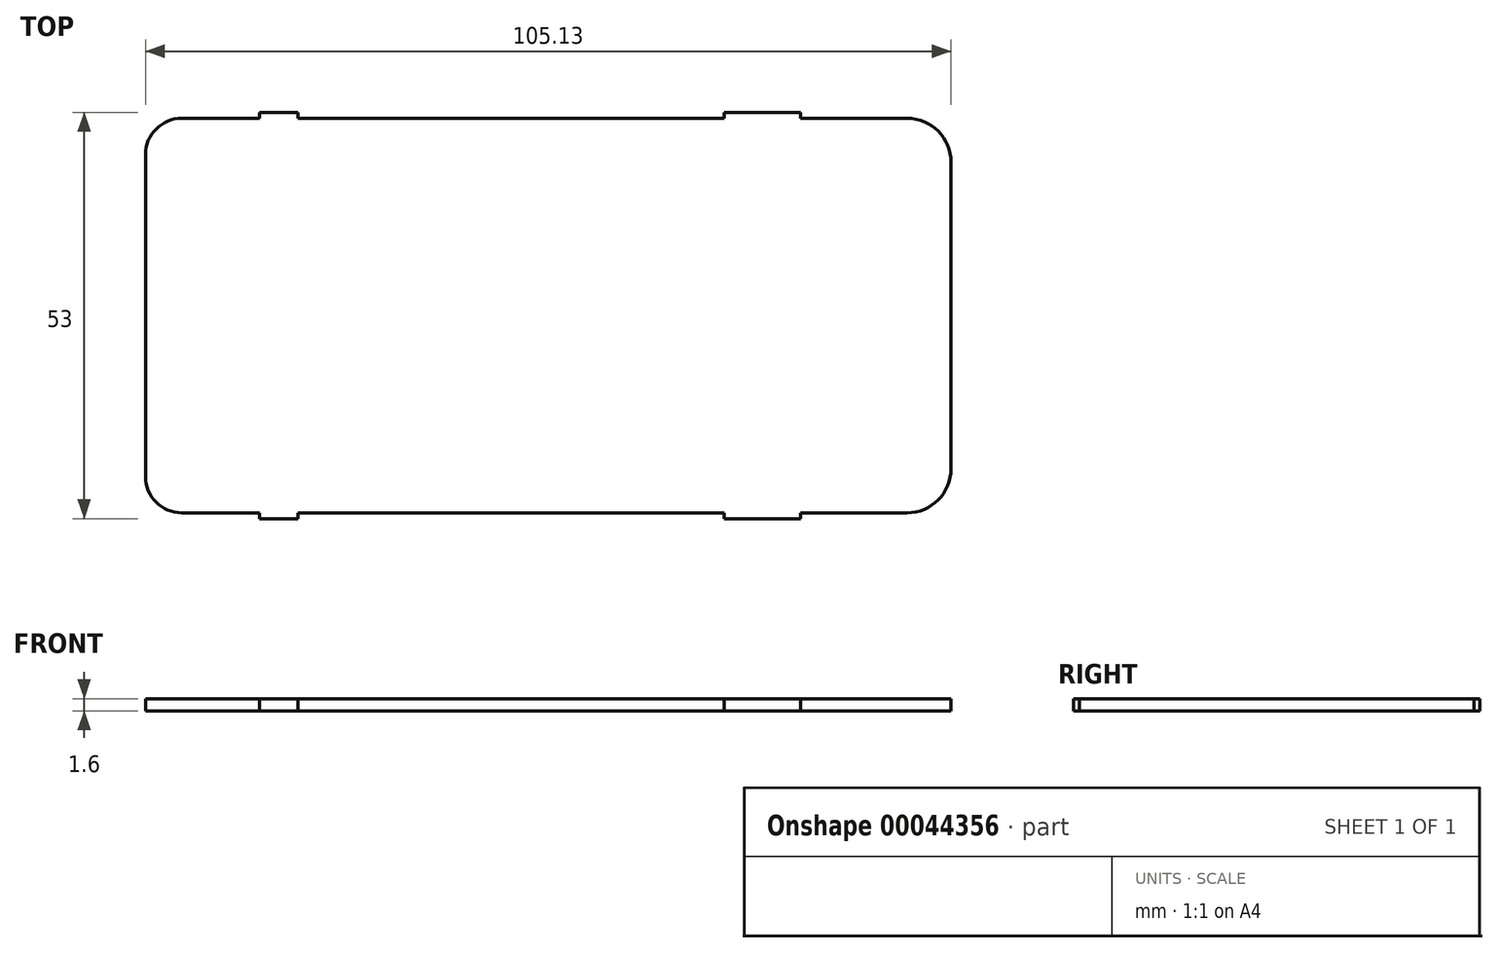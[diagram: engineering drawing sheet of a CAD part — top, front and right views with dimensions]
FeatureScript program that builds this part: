
annotation { "Feature Type Name" : "Feature", "Feature Type Description" : "" }
export const myFeature = defineFeature(function(context is Context, id is Id, definition is map)
    precondition{}
    {
        {
            var Q0;
            Q0=qCreatedBy(makeId("Top.planeOp"),FACE);
            var sketch = newSketch(context, id + "F0", { "sketchPlane" : qUnion([Q0])});
            skLineSegment(sketch, "E0", {"start": v(-46.45, 26.5) * mm, "end": v(-46.45, 25) * mm});
            skLineSegment(sketch, "E1", {"start": v(-46.45, -26.5) * mm, "end": v(-46.45, -25) * mm});
            skLineSegment(sketch, "E2", {"start": v(-50.45, -21) * mm, "end": v(-51.95, -21) * mm});
            skLineSegment(sketch, "E3", {"start": v(-50.45, 21) * mm, "end": v(-51.95, 21) * mm});
            skLineSegment(sketch, "E4", {"start": v(48.18, 25) * mm, "end": v(48.18, 26.5) * mm});
            skLineSegment(sketch, "E5", {"start": v(53.18, 20) * mm, "end": v(54.68, 20) * mm});
            skLineSegment(sketch, "E6", {"start": v(54.68, -20) * mm, "end": v(53.18, -20) * mm});
            skLineSegment(sketch, "E7", {"start": v(48.18, -26.5) * mm, "end": v(48.18, -25) * mm});
            skLineSegment(sketch, "E8", {"start": v(-46.45, -25.75) * mm, "end": v(48.18, -25.75) * mm});
            skLineSegment(sketch, "E9", {"start": v(-46.45, 25.75) * mm, "end": v(48.18, 25.75) * mm});
            skLineSegment(sketch, "E10", {"start": v(-51.2, 21) * mm, "end": v(-51.2, -21) * mm});
            skArc(sketch, "E11", {"start": v(-51.2, 21) * mm, "mid": v(-49.81, 24.36) * mm, "end": v(-46.45, 25.75) * mm});
            skArc(sketch, "E12", {"start": v(-51.2, -21) * mm, "mid": v(-49.81, -24.36) * mm, "end": v(-46.45, -25.75) * mm});
            skLineSegment(sketch, "E13", {"start": v(53.93, 20) * mm, "end": v(53.93, -20) * mm});
            skArc(sketch, "E14", {"start": v(48.18, -25.75) * mm, "mid": v(52.24, -24.07) * mm, "end": v(53.93, -20) * mm});
            skArc(sketch, "E15", {"start": v(53.93, 20) * mm, "mid": v(52.24, 24.07) * mm, "end": v(48.18, 25.75) * mm});
            skLineSegment(sketch, "E16", {"start": v(-36.31, 26.5) * mm, "end": v(-36.31, -26.5) * mm});
            skLineSegment(sketch, "E17", {"start": v(-36.31, -26.5) * mm, "end": v(-31.31, -26.5) * mm});
            skLineSegment(sketch, "E18", {"start": v(-31.31, -26.5) * mm, "end": v(-31.31, 26.5) * mm});
            skLineSegment(sketch, "E19", {"start": v(-31.31, 26.5) * mm, "end": v(-36.31, 26.5) * mm});
            skLineSegment(sketch, "E20", {"start": v(24.3, 26.5) * mm, "end": v(24.3, -26.5) * mm});
            skLineSegment(sketch, "E21", {"start": v(24.3, -26.5) * mm, "end": v(34.3, -26.5) * mm});
            skLineSegment(sketch, "E22", {"start": v(34.3, -26.5) * mm, "end": v(34.3, 26.5) * mm});
            skLineSegment(sketch, "E23", {"start": v(34.3, 26.5) * mm, "end": v(24.3, 26.5) * mm});
            skSolve(sketch);
        }
        {
            var Q0;
            {var subQ3=sQuery(id+"F0.wireOp",EDGE,"E8");var subQ5=sQuery(id+"F0.wireOp",EDGE,"E18");var subQ7=makeQuery(id+"F0.imprint","INTERSECT",VERTEX,{"derivedFrom":[subQ3,subQ5]});Q0=makeQuery(id+"F0.imprint","IMPRINT",FACE,{"disambiguationData":[TD([[makeQuery(id+"F0.imprint","IMPRINT",EDGE,{"disambiguationData":[TD([[subQ7,-1.0]])],"derivedFrom":subQ3}),1.0]])]});}
            var Q1;
            {var subQ3=sQuery(id+"F0.wireOp",EDGE,"E8");var subQ5=sQuery(id+"F0.wireOp",EDGE,"E20");var subQ7=makeQuery(id+"F0.imprint","INTERSECT",VERTEX,{"derivedFrom":[subQ3,subQ5]});Q1=makeQuery(id+"F0.imprint","IMPRINT",FACE,{"disambiguationData":[TD([[makeQuery(id+"F0.imprint","IMPRINT",EDGE,{"disambiguationData":[TD([[subQ7,-1.0]])],"derivedFrom":subQ3}),1.0]])]});}
            var Q2;
            Q2=makeQuery(id+"F0.imprint","IMPRINT",FACE,{"disambiguationData":[TD([[makeQuery(id+"F0.imprint","IMPRINT",EDGE,{"derivedFrom":sQuery(id+"F0.wireOp",EDGE,"E13")}),-1.0]])]});
            var Q3;
            {var subQ0=sQuery(id+"F0.wireOp",EDGE,"E23");Q3=makeQuery(id+"F0.imprint","IMPRINT",FACE,{"disambiguationData":[TD([[makeQuery(id+"F0.imprint","IMPRINT",EDGE,{"derivedFrom":subQ0}),1.0]])]});}
            var Q4;
            {var subQ3=sQuery(id+"F0.wireOp",EDGE,"E21");Q4=makeQuery(id+"F0.imprint","IMPRINT",FACE,{"disambiguationData":[TD([[makeQuery(id+"F0.imprint","IMPRINT",EDGE,{"derivedFrom":subQ3}),1.0]])]});}
            var Q5;
            {var subQ3=sQuery(id+"F0.wireOp",EDGE,"E17");Q5=makeQuery(id+"F0.imprint","IMPRINT",FACE,{"disambiguationData":[TD([[makeQuery(id+"F0.imprint","IMPRINT",EDGE,{"derivedFrom":subQ3}),1.0]])]});}
            var Q6;
            {var subQ3=sQuery(id+"F0.wireOp",EDGE,"E8");var subQ5=sQuery(id+"F0.wireOp",EDGE,"E16");var subQ7=makeQuery(id+"F0.imprint","INTERSECT",VERTEX,{"derivedFrom":[subQ3,subQ5]});Q6=makeQuery(id+"F0.imprint","IMPRINT",FACE,{"disambiguationData":[TD([[makeQuery(id+"F0.imprint","IMPRINT",EDGE,{"disambiguationData":[TD([[subQ7,-1.0]])],"derivedFrom":subQ3}),1.0]])]});}
            var Q7;
            Q7=makeQuery(id+"F0.imprint","IMPRINT",FACE,{"disambiguationData":[TD([[makeQuery(id+"F0.imprint","IMPRINT",EDGE,{"derivedFrom":sQuery(id+"F0.wireOp",EDGE,"E10")}),1.0]])]});
            var Q8;
            {var subQ0=sQuery(id+"F0.wireOp",EDGE,"E19");Q8=makeQuery(id+"F0.imprint","IMPRINT",FACE,{"disambiguationData":[TD([[makeQuery(id+"F0.imprint","IMPRINT",EDGE,{"derivedFrom":subQ0}),1.0]])]});}
            extrude(context, id + "F1", {"entities" : qUnion([Q0, Q1, Q2, Q3, Q4, Q5, Q6, Q7, Q8]), "depth" : 1.6 * mm});
        }
    });
